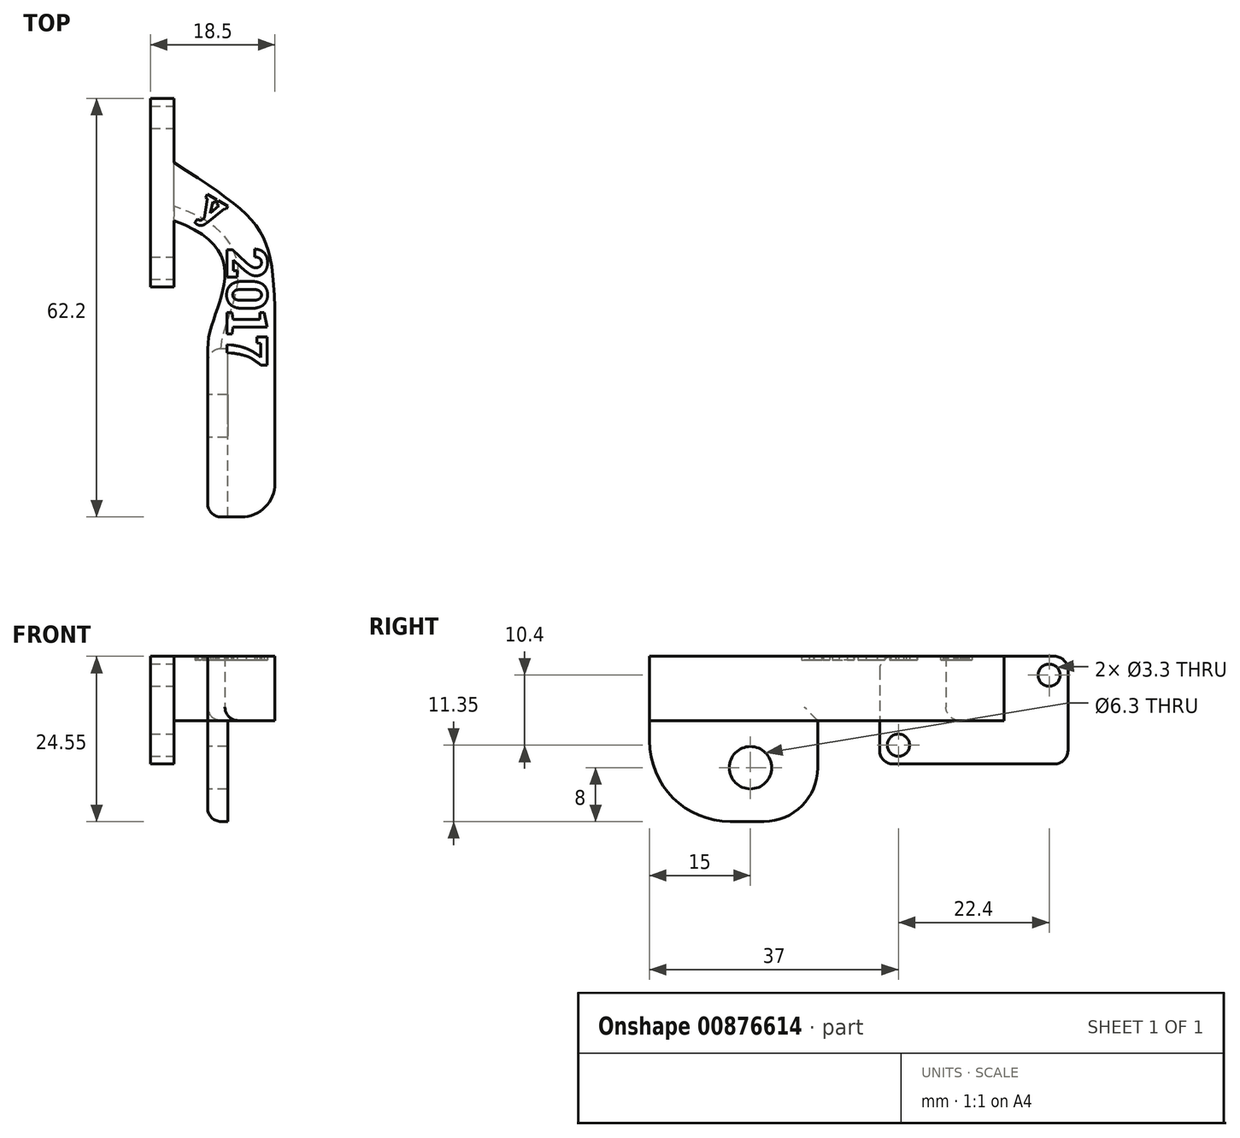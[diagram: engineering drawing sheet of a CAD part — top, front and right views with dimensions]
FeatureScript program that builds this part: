
annotation { "Feature Type Name" : "Feature", "Feature Type Description" : "" }
export const myFeature = defineFeature(function(context is Context, id is Id, definition is map)
    precondition{}
    {
        {
            var Q0;
            Q0=qCreatedBy(makeId("Top.planeOp"),FACE);
            var sketch = newSketch(context, id + "F0", { "sketchPlane" : qUnion([Q0])});
            skLineSegment(sketch, "E0.bottom", {"start": v(0, 0) * mm, "end": v(-3.5, 0) * mm});
            skLineSegment(sketch, "E0.top", {"start": v(0, 28) * mm, "end": v(-3.5, 28) * mm});
            skLineSegment(sketch, "E0.left", {"start": v(0, 0) * mm, "end": v(0, 28) * mm});
            skLineSegment(sketch, "E0.right", {"start": v(-3.5, 0) * mm, "end": v(-3.5, 28) * mm});
            skLineSegment(sketch, "E1.bottom", {"start": v(0, 9.85) * mm, "end": v(8.5, 9.85) * mm});
            skLineSegment(sketch, "E1.top", {"start": v(0, 15.85) * mm, "end": v(8.5, 15.85) * mm});
            skLineSegment(sketch, "E1.left", {"start": v(0, 9.85) * mm, "end": v(0, 15.85) * mm});
            skLineSegment(sketch, "E1.right", {"start": v(8.5, 9.85) * mm, "end": v(8.5, 15.85) * mm});
            skLineSegment(sketch, "E2", {"start": v(8.5, 9.85) * mm, "end": v(8.5, -34.2) * mm});
            skLineSegment(sketch, "E3", {"start": v(8.5, -34.2) * mm, "end": v(5, -34.2) * mm});
            skLineSegment(sketch, "E4", {"start": v(5, -34.2) * mm, "end": v(5, 9.85) * mm});
            skLineSegment(sketch, "E5.bottom", {"start": v(8.5, -34.2) * mm, "end": v(14.5, -34.2) * mm});
            skLineSegment(sketch, "E5.left", {"start": v(8.5, -34.2) * mm, "end": v(8.5, 0) * mm});
            skLineSegment(sketch, "E5.right", {"start": v(14.5, -34.2) * mm, "end": v(14.5, -9.2) * mm});
            skLineSegment(sketch, "E6", {"start": v(14.5, -9.2) * mm, "end": v(8.5, -9.2) * mm});
            skSolve(sketch);
        }
        {
            var Q0;
            Q0=qCreatedBy(makeId("Right.planeOp"),FACE);
            var sketch = newSketch(context, id + "F1", { "sketchPlane" : qUnion([Q0])});
            skLineSegment(sketch, "E7.bottom", {"start": v(0, 0) * mm, "end": v(28, 0) * mm});
            skLineSegment(sketch, "E7.top", {"start": v(0, -6.45) * mm, "end": v(28, -6.45) * mm});
            skCircle(sketch, "E8", {"center": v(2.8, -3.65) * mm, "radius": 1.65 * mm});
            skCircle(sketch, "E9", {"center": v(25.2, 6.75) * mm, "radius": 1.65 * mm});
            skCircle(sketch, "E10", {"center": v(-19.2, -7) * mm, "radius": 3.15 * mm});
            skLineSegment(sketch, "E11.bottom", {"start": v(-17.2, -15) * mm, "end": v(-22.2, -15) * mm});
            skLineSegment(sketch, "E11.left", {"start": v(-9.2, -7) * mm, "end": v(-9.2, 0) * mm});
            skLineSegment(sketch, "E11.right", {"start": v(-34.2, -3) * mm, "end": v(-34.2, 0) * mm});
            skLineSegment(sketch, "E12", {"start": v(-34.2, 0) * mm, "end": v(-34.2, 9.55) * mm});
            skLineSegment(sketch, "E13", {"start": v(-34.2, 9.55) * mm, "end": v(-9.2, 9.55) * mm});
            skLineSegment(sketch, "E14", {"start": v(-9.2, 9.55) * mm, "end": v(-9.2, 0) * mm});
            skCircle(sketch, "E15", {"center": v(-19.2, -7) * mm, "radius": 5 * mm, "construction": true});
            skLineSegment(sketch, "E16", {"start": v(3.84, -2) * mm, "end": v(-28.29, -2) * mm, "construction": true});
            skLineSegment(sketch, "E17", {"start": v(28, -6.45) * mm, "end": v(28, 9.55) * mm});
            skLineSegment(sketch, "E18", {"start": v(28, 9.55) * mm, "end": v(0, 9.55) * mm});
            skLineSegment(sketch, "E19", {"start": v(0, 9.55) * mm, "end": v(0, -6.45) * mm});
            skLineSegment(sketch, "E20", {"start": v(0, 9.55) * mm, "end": v(-9.2, 9.55) * mm});
            skLineSegment(sketch, "E21", {"start": v(0, -6.45) * mm, "end": v(-9.2, -6.45) * mm});
            skPoint(sketch, "E22.visualSharp", {"position": v(-9.2, -15) * mm});
            skArc(sketch, "E22.filletArc", {"start": v(-17.2, -15) * mm, "mid": v(-11.54, -12.66) * mm, "end": v(-9.2, -7) * mm});
            skPoint(sketch, "E23.visualSharp", {"position": v(-34.2, -15) * mm});
            skArc(sketch, "E23.filletArc", {"start": v(-34.2, -3) * mm, "mid": v(-30.69, -11.49) * mm, "end": v(-22.2, -15) * mm});
            skLineSegment(sketch, "E24", {"start": v(-34.2, 0) * mm, "end": v(-9.2, 0) * mm});
            skSolve(sketch);
        }
        {
            var Q0;
            {var subQ2=sQuery(id+"F1.wireOp",EDGE,"E7.bottom");Q0=makeQuery(id+"F1.imprint","IMPRINT",FACE,{"disambiguationData":[TD([[makeQuery(id+"F1.imprint","IMPRINT",EDGE,{"derivedFrom":subQ2}),1.0]])]});}
            var Q1;
            {var subQ1=sQuery(id+"F1.wireOp",EDGE,"E7.bottom");Q1=makeQuery(id+"F1.imprint","IMPRINT",FACE,{"disambiguationData":[TD([[makeQuery(id+"F1.imprint","IMPRINT",EDGE,{"derivedFrom":subQ1}),-1.0]])]});}
            extrude(context, id + "F2", {"entities" : qUnion([Q0, Q1]), "oppositeDirection" : true, "depth" : 3.5 * mm, "offsetDistance" : 25 * mm});
        }
        {
            var Q0;
            Q0=qCreatedBy(makeId("Top.planeOp"),FACE);
            var sketch = newSketch(context, id + "F3", { "sketchPlane" : qUnion([Q0])});
            skFitSpline(sketch, "E25", {"points": [v(15, -9.2) * mm, v(0, 18.48) * mm], "startDerivative": vector(0, 54.1) * mm, "endDerivative": vector(-44.18, 28.94) * mm});
            skFitSpline(sketch, "E26", {"points": [v(0, 9.85) * mm, v(5, -9.2) * mm], "startDerivative": vector(40.03, -14.8) * mm, "endDerivative": vector(0, -18.83) * mm});
            skLineSegment(sketch, "E27", {"start": v(0, 9.85) * mm, "end": v(0, 18.48) * mm});
            skLineSegment(sketch, "E28", {"start": v(5, -9.2) * mm, "end": v(15, -9.2) * mm});
            skSolve(sketch);
        }
        {
            var Q0;
            Q0=makeQuery(id+"F3.imprint","IMPRINT",FACE,{"disambiguationData":[TD([[makeQuery(id+"F3.imprint","IMPRINT",EDGE,{"derivedFrom":sQuery(id+"F3.wireOp",EDGE,"E25")}),1.0]])]});
            extrude(context, id + "F4", {"entities" : qUnion([Q0]), "operationType" : NewBodyOperationType.ADD, "depth" : 9.55 * mm, "offsetDistance" : 25 * mm});
        }
        {
            var Q0;
            {var subQ3=sQuery(id+"F1.wireOp",EDGE,"E12");Q0=makeQuery(id+"F1.imprint","IMPRINT",FACE,{"disambiguationData":[TD([[makeQuery(id+"F1.imprint","IMPRINT",EDGE,{"derivedFrom":subQ3}),-1.0]])]});}
            extrude(context, id + "F5", {"entities" : qUnion([Q0]), "operationType" : NewBodyOperationType.ADD, "depth" : 15 * mm, "offsetDistance" : 25 * mm, "hasSecondDirection" : true, "secondDirectionOppositeDirection" : false, "secondDirectionDepth" : 5 * mm});
        }
        {
            var Q0;
            Q0=makeQuery(id+"F1.imprint","IMPRINT",FACE,{"disambiguationData":[TD([[makeQuery(id+"F1.imprint","IMPRINT",EDGE,{"derivedFrom":sQuery(id+"F1.wireOp",EDGE,"E10")}),-1.0]])]});
            extrude(context, id + "F6", {"entities" : qUnion([Q0]), "operationType" : NewBodyOperationType.ADD, "depth" : 8 * mm, "offsetDistance" : 25 * mm, "hasSecondDirection" : true, "secondDirectionOppositeDirection" : false, "secondDirectionDepth" : 5 * mm});
        }
        {
            var Q0;
            Q0=makeQuery(id+"F2.opExtrude","SWEPT_EDGE",EDGE,{"disambiguationData":[OSD([sQuery(id+"F1.wireOp",EDGE,"E7.top"),sQuery(id+"F1.wireOp",EDGE,"E17")])]});
            var Q1;
            Q1=makeQuery(id+"F2.opExtrude","SWEPT_EDGE",EDGE,{"disambiguationData":[OSD([sQuery(id+"F1.wireOp",EDGE,"E7.top"),sQuery(id+"F1.wireOp",EDGE,"E19"),sQuery(id+"F1.wireOp",EDGE,"E21")])]});
            var Q2;
            Q2=makeQuery(id+"F2.opExtrude","SWEPT_EDGE",EDGE,{"disambiguationData":[OSD([sQuery(id+"F1.wireOp",EDGE,"E18"),sQuery(id+"F1.wireOp",EDGE,"E19"),sQuery(id+"F1.wireOp",EDGE,"E20")])]});
            var Q3;
            Q3=makeQuery(id+"F2.opExtrude","SWEPT_EDGE",EDGE,{"disambiguationData":[OSD([sQuery(id+"F1.wireOp",EDGE,"E17"),sQuery(id+"F1.wireOp",EDGE,"E18")])]});
            fillet(context, id + "F7", {"entities" : qUnion([Q0, Q1, Q2, Q3]), "radius" : 2 * mm, "tangentPropagation" : true, "allowEdgeOverflow" : false});
        }
        {
            var Q0;
            Q0=makeQuery(id+"F4.opExtrude","CAP_EDGE",EDGE,{"disambiguationData":[OSD([sQuery(id+"F3.wireOp",EDGE,"E26")])],"isStart":true});
            var Q1;
            Q1=makeQuery(id+"F6.opExtrude","CAP_EDGE",EDGE,{"disambiguationData":[OSD([sQuery(id+"F1.wireOp",EDGE,"E11.left")])],"isStart":true});
            var Q2;
            Q2=makeQuery(id+"F6.opExtrude","CAP_EDGE",EDGE,{"disambiguationData":[OSD([sQuery(id+"F1.wireOp",EDGE,"E22.filletArc")])],"isStart":true});
            var Q3;
            Q3=makeQuery(id+"F6.opExtrude","CAP_EDGE",EDGE,{"disambiguationData":[OSD([sQuery(id+"F1.wireOp",EDGE,"E11.bottom")])],"isStart":true});
            var Q4;
            Q4=makeQuery(id+"F6.opExtrude","CAP_EDGE",EDGE,{"disambiguationData":[OSD([sQuery(id+"F1.wireOp",EDGE,"E23.filletArc")])],"isStart":true});
            var Q5;
            Q5=makeQuery(id+"F6.boolean.opBoolean","MERGE",EDGE,{"derivedFrom":[makeQuery(id+"F5.opExtrude","CAP_EDGE",EDGE,{"disambiguationData":[OSD([sQuery(id+"F1.wireOp",EDGE,"E12")])],"isStart":true}),makeQuery(id+"F6.opExtrude","CAP_EDGE",EDGE,{"disambiguationData":[OSD([sQuery(id+"F1.wireOp",EDGE,"E11.right")])],"isStart":true})]});
            fillet(context, id + "F8", {"entities" : qUnion([Q0, Q1, Q2, Q3, Q4, Q5]), "radius" : 2 * mm, "tangentPropagation" : true, "allowEdgeOverflow" : false});
        }
        {
            var Q0;
            Q0=makeQuery(id+"F5.opExtrude","CAP_EDGE",EDGE,{"disambiguationData":[OSD([sQuery(id+"F1.wireOp",EDGE,"E12")])],"isStart":false});
            fillet(context, id + "F9", {"entities" : qUnion([Q0]), "radius" : 5 * mm, "tangentPropagation" : true, "allowEdgeOverflow" : false});
        }
        {
            var Q0;
            Q0=qCreatedBy(makeId("Top.planeOp"),FACE);
            var sketch = newSketch(context, id + "F10", { "sketchPlane" : qUnion([Q0])});
            skText(sketch, "E29", { "text": "2017", "fontName": "RobotoSlab-Bold.ttf"});
            skText(sketch, "E30", { "text": "y", "fontName": "RobotoSlab-Bold.ttf"});
            const initialGuessF10  = {"E29": [0.0079, 0.00581, 0, -1, 0.006], "E30": [0.00325, 0.01092, 0.86603, -0.5, 0.0045]};
            skSetInitialGuess(sketch, initialGuessF10);
            skSolve(sketch);
        }
        {
            var Q0;
            Q0=makeQuery(id+"F10.imprint","IMPRINT",FACE,{"disambiguationData":[TD([[makeQuery(id+"F10.imprint","IMPRINT",EDGE,{"derivedFrom":sQuery(id+"F10.wireOp",EDGE,"E30.sketch_text.stroke-0")}),-1.0]])]});
            var Q1;
            Q1=makeQuery(id+"F10.imprint","IMPRINT",FACE,{"disambiguationData":[TD([[makeQuery(id+"F10.imprint","IMPRINT",EDGE,{"derivedFrom":sQuery(id+"F10.wireOp",EDGE,"E29.sketch_text.stroke-0")}),-1.0]])]});
            var Q2;
            Q2=makeQuery(id+"F10.imprint","IMPRINT",FACE,{"disambiguationData":[TD([[makeQuery(id+"F10.imprint","IMPRINT",EDGE,{"derivedFrom":sQuery(id+"F10.wireOp",EDGE,"E29.sketch_text.stroke-23")}),-1.0]])]});
            var Q3;
            Q3=makeQuery(id+"F10.imprint","IMPRINT",FACE,{"disambiguationData":[TD([[makeQuery(id+"F10.imprint","IMPRINT",EDGE,{"derivedFrom":sQuery(id+"F10.wireOp",EDGE,"E29.sketch_text.stroke-43")}),-1.0]])]});
            var Q4;
            Q4=makeQuery(id+"F10.imprint","IMPRINT",FACE,{"disambiguationData":[TD([[makeQuery(id+"F10.imprint","IMPRINT",EDGE,{"derivedFrom":sQuery(id+"F10.wireOp",EDGE,"E29.sketch_text.stroke-53")}),-1.0]])]});
            extrude(context, id + "F11", {"entities" : qUnion([Q0, Q1, Q2, Q3, Q4]), "operationType" : NewBodyOperationType.REMOVE, "depth" : 20 * mm, "offsetDistance" : 25 * mm, "hasSecondDirection" : true, "secondDirectionOppositeDirection" : false, "secondDirectionDepth" : 9 * mm});
        }
    });
